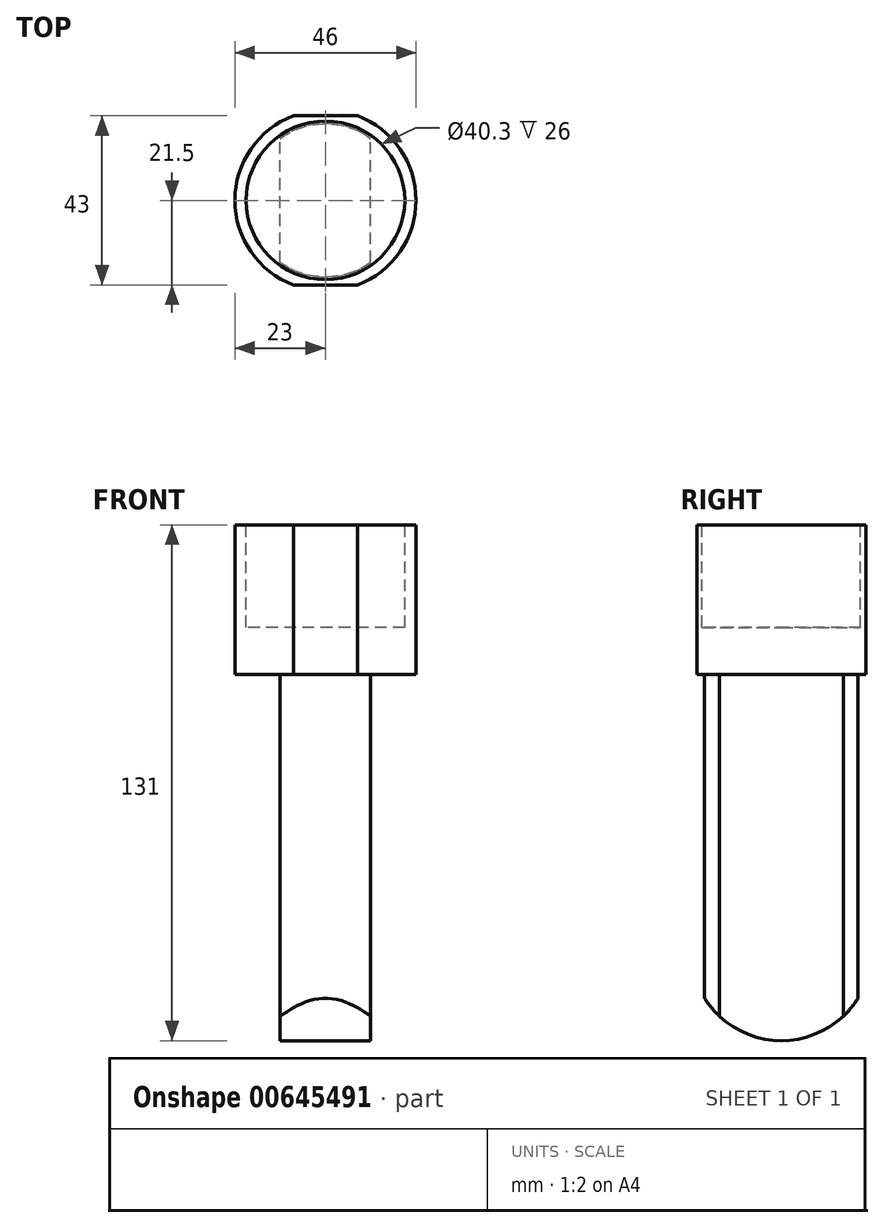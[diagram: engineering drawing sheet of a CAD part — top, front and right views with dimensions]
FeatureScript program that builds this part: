
annotation { "Feature Type Name" : "Feature", "Feature Type Description" : "" }
export const myFeature = defineFeature(function(context is Context, id is Id, definition is map)
    precondition{}
    {
        {
            var Q0;
            Q0=qCreatedBy(makeId("Top.planeOp"),FACE);
            var sketch = newSketch(context, id + "F0", { "sketchPlane" : qUnion([Q0])});
            skArc(sketch, "E0", {"start": v(-8.17, 21.5) * mm, "mid": v(-23, 0) * mm, "end": v(-8.17, -21.5) * mm});
            skLineSegment(sketch, "E1", {"start": v(-8.17, 21.5) * mm, "end": v(8.17, 21.5) * mm});
            skLineSegment(sketch, "E2.MirrorCS", {"start": v(-8.17, -21.5) * mm, "end": v(8.17, -21.5) * mm});
            skArc(sketch, "E3.trimOffspring", {"start": v(8.17, -21.5) * mm, "mid": v(23, 0) * mm, "end": v(8.17, 21.5) * mm});
            skSolve(sketch);
        }
        {
            var Q0;
            Q0=makeQuery(id+"F0.imprint","IMPRINT",FACE,{"disambiguationData":[TD([[makeQuery(id+"F0.imprint","IMPRINT",EDGE,{"derivedFrom":sQuery(id+"F0.wireOp",EDGE,"E0")}),1.0]])]});
            extrude(context, id + "F1", {"entities" : qUnion([Q0]), "depth" : 38 * mm, "offsetDistance" : 25 * mm});
        }
        {
            var Q0;
            Q0=makeQuery(id+"F1.opExtrude","CAP_FACE",FACE,{"disambiguationData":[OSD([sQuery(id+"F0.wireOp",EDGE,"E0"),sQuery(id+"F0.wireOp",EDGE,"E1"),sQuery(id+"F0.wireOp",EDGE,"E2.MirrorCS"),sQuery(id+"F0.wireOp",EDGE,"E3.trimOffspring")])],"isStart":false});
            var sketch = newSketch(context, id + "F2", { "sketchPlane" : qUnion([Q0])});
            skCircle(sketch, "E4", {"center": v(0, 0) * mm, "radius": 20.15 * mm});
            skSolve(sketch);
        }
        {
            var Q0;
            Q0=makeQuery(id+"F2.imprint","IMPRINT",FACE,{"disambiguationData":[TD([[makeQuery(id+"F2.imprint","IMPRINT",EDGE,{"derivedFrom":sQuery(id+"F2.wireOp",EDGE,"E4")}),1.0]])]});
            extrude(context, id + "F3", {"entities" : qUnion([Q0]), "operationType" : NewBodyOperationType.REMOVE, "oppositeDirection" : true, "depth" : 26 * mm, "offsetDistance" : 25 * mm});
        }
        {
            var Q0;
            Q0=makeQuery(id+"F1.opExtrude","CAP_FACE",FACE,{"disambiguationData":[OSD([sQuery(id+"F0.wireOp",EDGE,"E0"),sQuery(id+"F0.wireOp",EDGE,"E1"),sQuery(id+"F0.wireOp",EDGE,"E2.MirrorCS"),sQuery(id+"F0.wireOp",EDGE,"E3.trimOffspring")])],"isStart":true});
            var sketch = newSketch(context, id + "F4", { "sketchPlane" : qUnion([Q0])});
            skArc(sketch, "E5", {"start": v(-11.5, -15.75) * mm, "mid": v(0, -19.5) * mm, "end": v(11.5, -15.75) * mm});
            skLineSegment(sketch, "E6", {"start": v(-11.5, 15.75) * mm, "end": v(-11.5, -15.75) * mm});
            skLineSegment(sketch, "E7.MirrorCS", {"start": v(11.5, 15.75) * mm, "end": v(11.5, -15.75) * mm});
            skArc(sketch, "E8.trimOffspring", {"start": v(11.5, 15.75) * mm, "mid": v(0, 19.5) * mm, "end": v(-11.5, 15.75) * mm});
            skSolve(sketch);
        }
        {
            var Q0;
            Q0=makeQuery(id+"F4.imprint","IMPRINT",FACE,{"disambiguationData":[TD([[makeQuery(id+"F4.imprint","IMPRINT",EDGE,{"derivedFrom":sQuery(id+"F4.wireOp",EDGE,"E5")}),1.0]])]});
            extrude(context, id + "F5", {"entities" : qUnion([Q0]), "operationType" : NewBodyOperationType.ADD, "depth" : 93 * mm, "offsetDistance" : 25 * mm});
        }
        {
            var Q0;
            Q0=makeQuery(id+"F5.opExtrude","SWEPT_FACE",FACE,{"disambiguationData":[OSD([sQuery(id+"F4.wireOp",EDGE,"E7.MirrorCS")])]});
            var sketch = newSketch(context, id + "F6", { "sketchPlane" : qUnion([Q0])});
            skArc(sketch, "E9", {"start": v(-22.67, -73.89) * mm, "mid": v(-1.4, -92.96) * mm, "end": v(22.03, -76.61) * mm});
            skLineSegment(sketch, "E10", {"start": v(22.03, -76.61) * mm, "end": v(22.03, -100.07) * mm});
            skLineSegment(sketch, "E11", {"start": v(22.03, -100.07) * mm, "end": v(-22.67, -100.07) * mm});
            skLineSegment(sketch, "E12", {"start": v(-22.67, -100.07) * mm, "end": v(-22.67, -73.89) * mm});
            skSolve(sketch);
        }
        {
            var Q0;
            {var subQ0=sQuery(id+"F6.wireOp",EDGE,"E9");var subQ1=sQuery(id+"F4.wireOp",EDGE,"E7.MirrorCS");var subQ4=makeQuery(id+"F5.opExtrude","CAP_EDGE",EDGE,{"disambiguationData":[OSD([subQ1])],"isStart":false});var subQ5=makeQuery(id+"F6.imprint","INTERSECT",VERTEX,{"derivedFrom":[subQ4,subQ0]});Q0=makeQuery(id+"F6.imprint","IMPRINT",FACE,{"disambiguationData":[TD([[makeQuery(id+"F6.imprint","IMPRINT",EDGE,{"disambiguationData":[TD([[subQ5,1.0]])],"derivedFrom":subQ0}),-1.0]])]});}
            var Q1;
            {var subQ0=sQuery(id+"F6.wireOp",EDGE,"E9");var subQ1=sQuery(id+"F4.wireOp",EDGE,"E7.MirrorCS");var subQ4=makeQuery(id+"F5.opExtrude","CAP_EDGE",EDGE,{"disambiguationData":[OSD([subQ1])],"isStart":false});var subQ5=makeQuery(id+"F6.imprint","INTERSECT",VERTEX,{"derivedFrom":[subQ4,subQ0]});Q1=makeQuery(id+"F6.imprint","IMPRINT",FACE,{"disambiguationData":[TD([[makeQuery(id+"F6.imprint","IMPRINT",EDGE,{"disambiguationData":[TD([[subQ5,-1.0]])],"derivedFrom":subQ0}),-1.0]])]});}
            var Q2;
            {var subQ0=sQuery(id+"F6.wireOp",EDGE,"E10");Q2=makeQuery(id+"F6.imprint","IMPRINT",FACE,{"disambiguationData":[TD([[makeQuery(id+"F6.imprint","IMPRINT",EDGE,{"derivedFrom":subQ0}),-1.0]])]});}
            extrude(context, id + "F7", {"entities" : qUnion([Q0, Q1, Q2]), "operationType" : NewBodyOperationType.REMOVE, "endBound" : BoundingType.THROUGH_ALL, "oppositeDirection" : true, "depth" : 25 * mm, "offsetDistance" : 25 * mm});
        }
    });
